# Revit family: Haworth_Riverbend_StraightBench
name_source: partatom
category: Furniture
revit_build: Autodesk Revit 2018 (Build: 20170223_1515(x64)
units: mm (PartAtom-declared; Revit-internal decimal feet)

## family parameters
Always vertical = Yes
Cut with Voids When Loaded = No
OmniClass Number = 23.40.70.14.64.21
OmniClass Title = Systems Furniture
Room Calculation Point = No
Shared = No
Work Plane-Based = No

## types (8) — shared parameters
Actual Depth = 33"
Actual Height = 18"
Assembly Code = E2020200
Custom Size = No
Custom Width = No
Depth = 33"
Description = Haworth Riverbend Straight Bench
Front Finish = Haworth _ Plastic _ Black
Hardware Finish = Haworth _ Paint _ Plaster
Manufacturer = Haworth
Max. Depth = 33"
Max. Width = 67"
Min. Depth = 33"
Min. Width = 28"
Model = SMSN
Revision Number = 1
Size = Verify Final Dim. w/ Haworth
Standard Depths = 33 in.
Standard Heights = 31 in., 50 in.
Standard Widths = 28 in., 55 in., 67 in.
URL = http://www.haworth.com
URL - Product = http://www.haworth.com
Warranty = http://www.haworth.com

## per-type parameters (varying)
| type | Actual Width | High Back | Mid Back | No Back | Width |
| 33d 28w 31h - Mid Back | 28" | No | Yes | No | 28" |
| 33d 55w 31h - Mid Back | 55" | No | Yes | No | 55" |
| 33d 67w 31h - Mid Back | 67" | No | Yes | No | 67" |
| 33d 55w 50h - High Back | 55" | Yes | No | No | 55" |
| 33d 67w 50h - High Back | 67" | Yes | No | No | 67" |
| 33d 28w 18h - No Back | 28" | No | No | Yes | 28" |
| 33d 55w 18h - No Back | 55" | No | No | Yes | 55" |
| 33d 67w 18h - No Back | 67" | No | No | Yes | 67" |

## geometry (parser evidence)
native form markers: Sweep x4
no freeform markers — native parametric forms only
